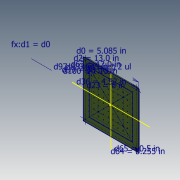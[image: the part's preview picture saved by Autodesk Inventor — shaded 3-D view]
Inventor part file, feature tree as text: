
AUTODESK INVENTOR PART (.ipt)
format: ipt  version: 2018.3 (Build 223284000, 284)  size: 231,936 bytes
history: native  units: in
note: dims shown in document units (in); Inventor stores cm internally (conversion verified against a paired STEP export)
features: hole x3, extrude x1, pattern_linear x1, fillet x1, sketch x1
ambient origin geometry x8: Origin, YZ Plane, XZ Plane, XY Plane, X Axis, Y Axis, Z Axis, Center Point
bodies: Solid1 (feature_tree)
feature tree (7):
  extrude  "Extrusion1"  Depth=0.5in
  hole  "Hole1"  [1 undecoded]
  pattern_linear  "Rectangular Pattern1"  Spacing1=0.23in  [1 undecoded]
  fillet  "Fillet2"  Radius=3.937in
  hole  "Hole6"  [1 undecoded]
  hole  "Hole10"  [1 undecoded]
  sketch  "Sketch4"  dims[d0=5.085in d1=5.085in d2=13.0in d4=0.23in d5=0.0in d6=0.17in d7=0.236in d8=0.248in d9=0.1in d10=90.0deg d11=0.346in d12=0.8108in d13=3.937in d15=1.13in d16=3.937in d18=1.13in d23=6.0in d36=4.52in d50=0.5in d63=12.0in d64=0.255in d65=0.5in d83=0.19in d84=0.472in d85=0.375in d86=0.25in d87=0.5635in d88=1.0in d89=0.8108in d97=1.29in d98=45.0deg d99=30.0deg d100=1.13in d115=0.165in d116=0.472in d117=0.409in d118=0.25in d119=90.0deg d120=0.559in d121=0.8108in]
note: 4 required parameter values undecoded (feature->parameter linkage not recoverable at this tier; creation-order binding heuristic only, values carry confidence <= 0.55)
